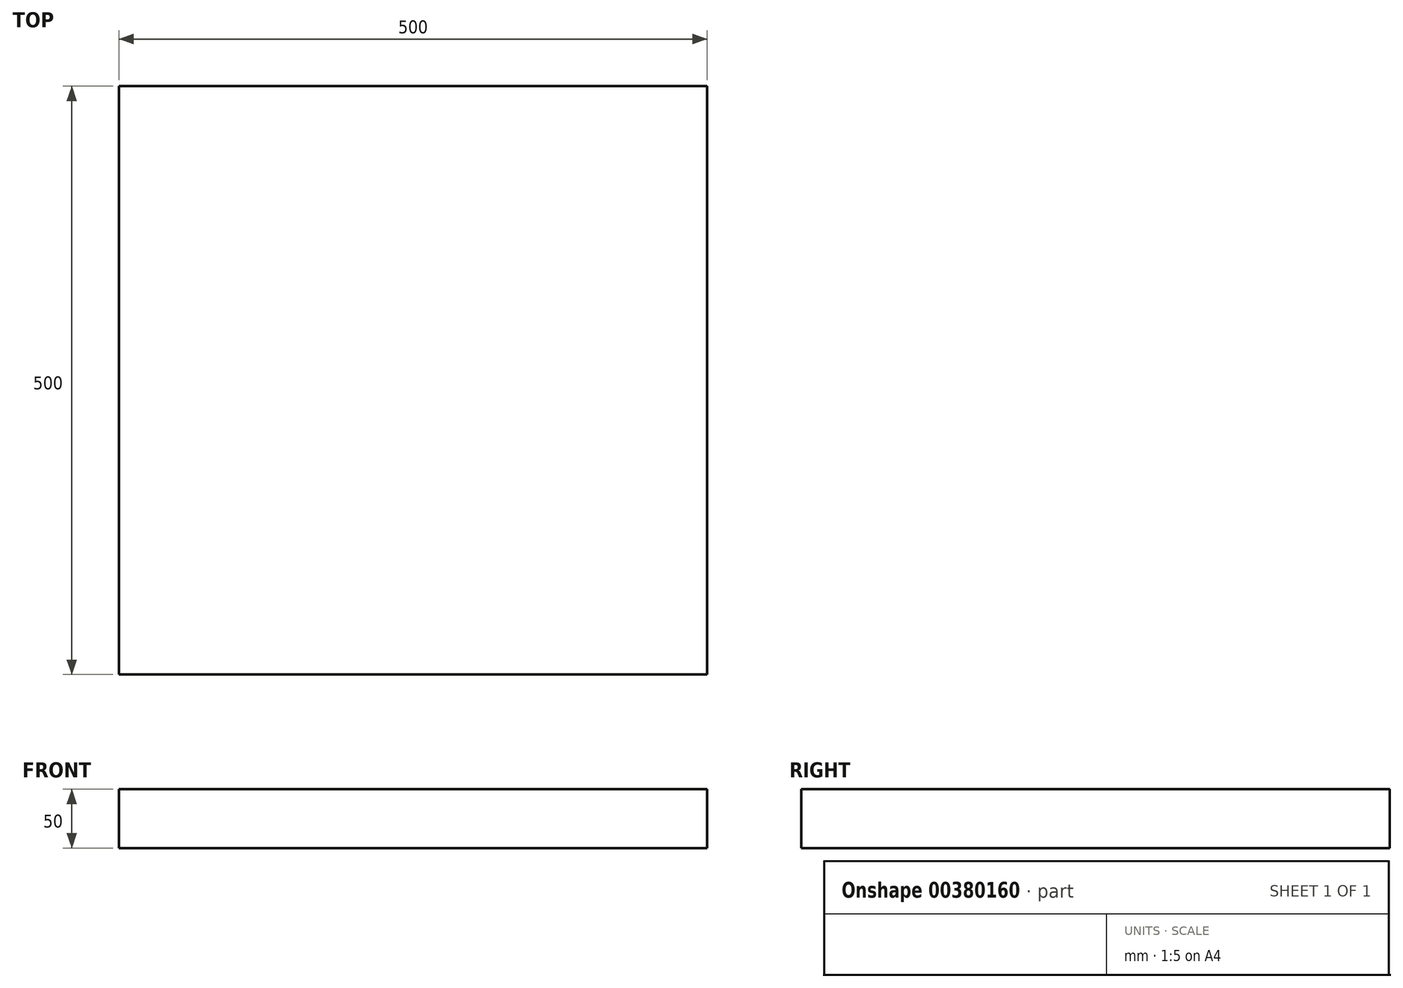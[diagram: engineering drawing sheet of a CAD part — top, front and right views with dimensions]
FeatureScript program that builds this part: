
annotation { "Feature Type Name" : "Feature", "Feature Type Description" : "" }
export const myFeature = defineFeature(function(context is Context, id is Id, definition is map)
    precondition{}
    {
        {
            var Q0;
            Q0=qCreatedBy(makeId("Top.planeOp"),FACE);
            var sketch = newSketch(context, id + "F0", { "sketchPlane" : qUnion([Q0])});
            skLineSegment(sketch, "E0.bottom", {"start": v(250, -250) * mm, "end": v(-250, -250) * mm});
            skLineSegment(sketch, "E0.top", {"start": v(250, 250) * mm, "end": v(-250, 250) * mm});
            skLineSegment(sketch, "E0.left", {"start": v(250, -250) * mm, "end": v(250, 250) * mm});
            skLineSegment(sketch, "E0.right", {"start": v(-250, -250) * mm, "end": v(-250, 250) * mm});
            skPoint(sketch, "E0.middle", {"position": v(0, 0) * mm});
            skSolve(sketch);
        }
        {
            var Q0;
            Q0 = qSketchRegion(id + "F0", true);
            extrude(context, id + "F1", {"entities" : qUnion([Q0]), "endBound" : BoundingType.SYMMETRIC, "depth" : 50 * mm});
        }
    });
